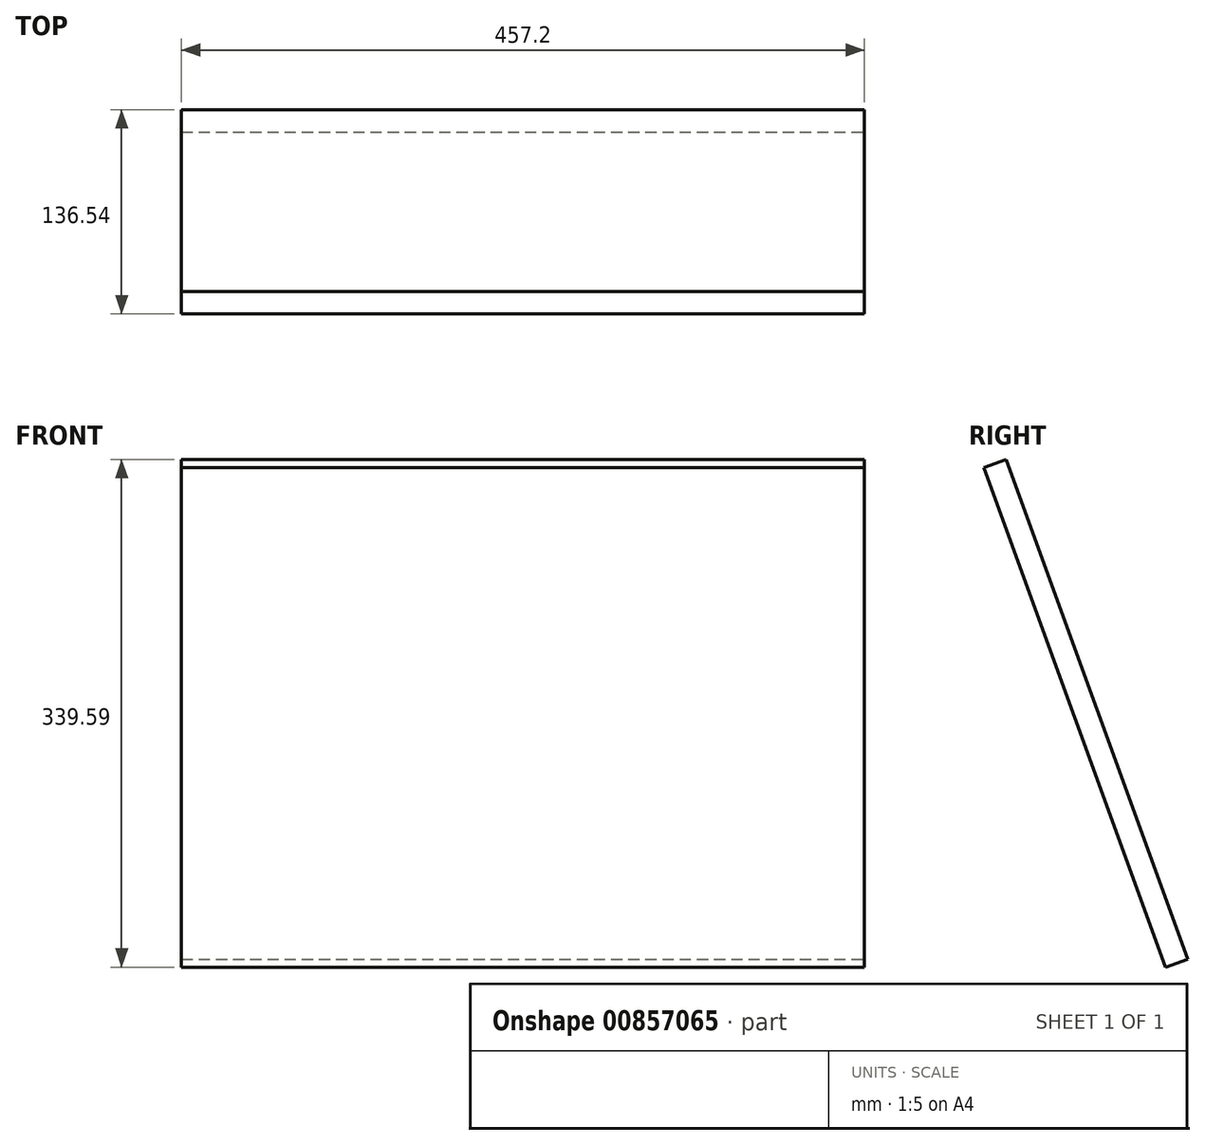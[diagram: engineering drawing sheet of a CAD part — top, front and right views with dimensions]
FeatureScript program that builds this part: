
annotation { "Feature Type Name" : "Feature", "Feature Type Description" : "" }
export const myFeature = defineFeature(function(context is Context, id is Id, definition is map)
    precondition{}
    {
        {
            var Q0;
            Q0=qCreatedBy(makeId("Top.planeOp"),FACE);
            var sketch = newSketch(context, id + "F0", { "sketchPlane" : qUnion([Q0])});
            skLineSegment(sketch, "E0.bottom", {"start": v(-228.6, 177.8) * mm, "end": v(228.6, 177.8) * mm});
            skLineSegment(sketch, "E0.top", {"start": v(-228.6, -177.8) * mm, "end": v(228.6, -177.8) * mm});
            skLineSegment(sketch, "E0.left", {"start": v(-228.6, 177.8) * mm, "end": v(-228.6, -177.8) * mm});
            skLineSegment(sketch, "E0.right", {"start": v(228.6, 177.8) * mm, "end": v(228.6, -177.8) * mm});
            skPoint(sketch, "E0.middle", {"position": v(0, 0) * mm});
            skLineSegment(sketch, "E1", {"start": v(76.2, 0) * mm, "end": v(-76.2, 0) * mm});
            skSolve(sketch);
        }
        {
            var Q0;
            Q0 = qSketchRegion(id + "F0", true);
            extrude(context, id + "F1", {"entities" : qUnion([Q0]), "depth" : 15.88 * mm, "offsetDistance" : 25.4 * mm});
        }
        {
            var Q0;
            Q0=makeQuery(id+"F1.opExtrude","SWEPT_BODY",BODY,{"disambiguationData":[OSD([sQuery(id+"F0.wireOp",EDGE,"E0.bottom"),sQuery(id+"F0.wireOp",EDGE,"E0.top"),sQuery(id+"F0.wireOp",EDGE,"E0.left"),sQuery(id+"F0.wireOp",EDGE,"E0.right")])]});
            var Q1;
            Q1=sQuery(id+"F0.wireOp",EDGE,"E1");
            var Q2;
            Q2=sQuery(id+"F0.wireOp",EDGE,"E1");
            transform(context, id + "F2", {"entities" : qUnion([Q0]), "transformType" : TransformType.ROTATION, "transformAxis" : qUnion([Q2]), "angle" : 70 * degree, "makeCopy" : false});
        }
    });
